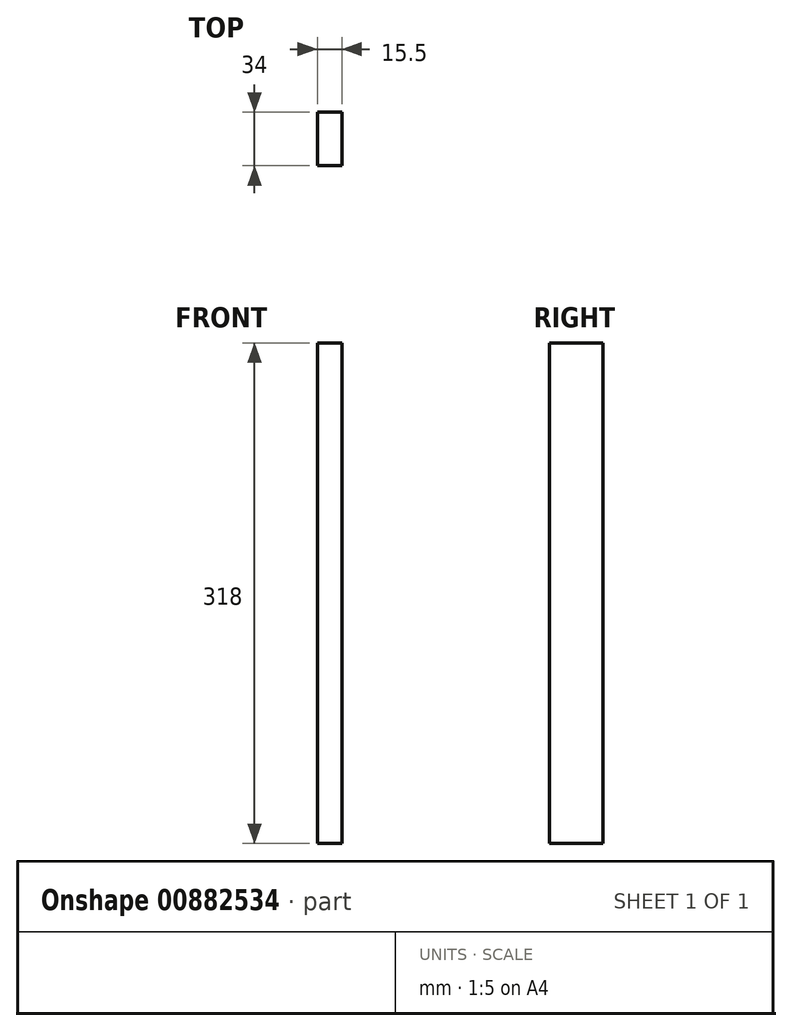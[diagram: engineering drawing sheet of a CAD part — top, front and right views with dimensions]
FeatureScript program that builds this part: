
annotation { "Feature Type Name" : "Feature", "Feature Type Description" : "" }
export const myFeature = defineFeature(function(context is Context, id is Id, definition is map)
    precondition{}
    {
        {
            var Q0;
            Q0=qCreatedBy(makeId("Top.planeOp"),FACE);
            var sketch = newSketch(context, id + "F0", { "sketchPlane" : qUnion([Q0])});
            skLineSegment(sketch, "E0.bottom", {"start": v(0, 0) * mm, "end": v(15.5, 0) * mm});
            skLineSegment(sketch, "E0.top", {"start": v(0, -34) * mm, "end": v(15.5, -34) * mm});
            skLineSegment(sketch, "E0.left", {"start": v(0, 0) * mm, "end": v(0, -34) * mm});
            skLineSegment(sketch, "E0.right", {"start": v(15.5, 0) * mm, "end": v(15.5, -34) * mm});
            skSolve(sketch);
        }
        {
            var Q0;
            Q0=qSketchRegion(id+"F0",true);
            extrude(context, id + "F1", {"entities" : qUnion([Q0]), "depth" : 318 * mm, "offsetDistance" : 25 * mm});
        }
    });
